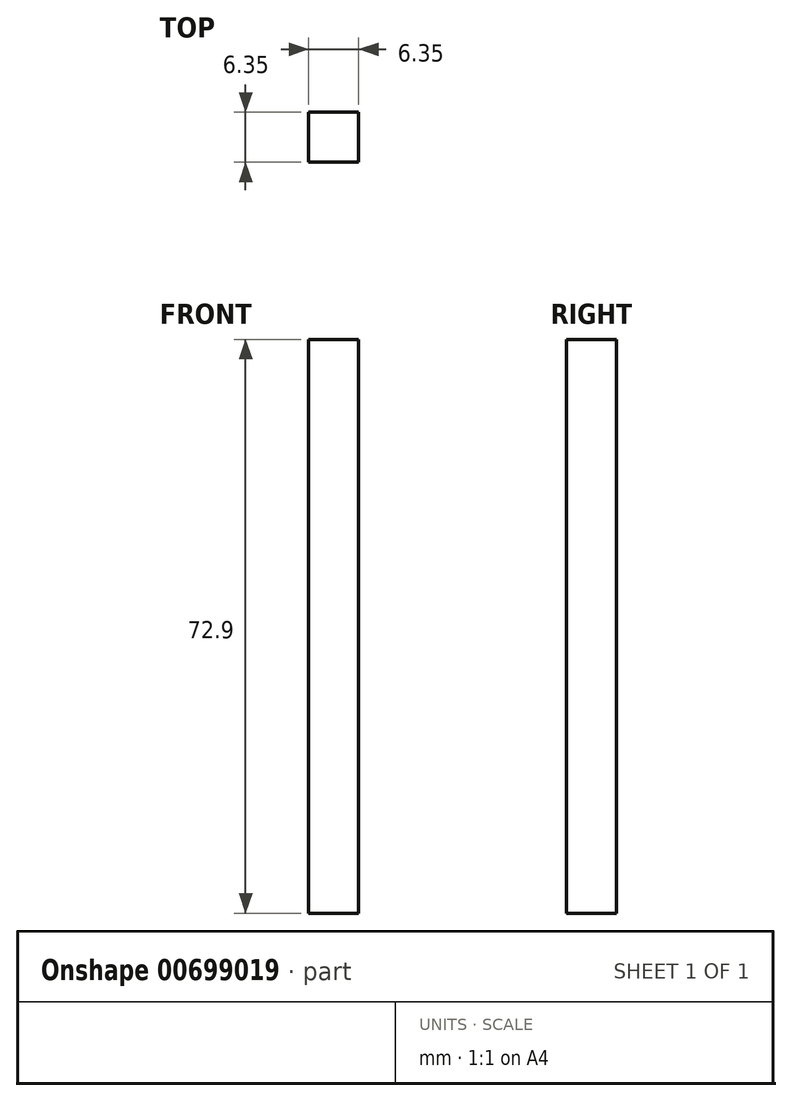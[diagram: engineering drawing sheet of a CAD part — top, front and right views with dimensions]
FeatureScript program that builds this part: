
annotation { "Feature Type Name" : "Feature", "Feature Type Description" : "" }
export const myFeature = defineFeature(function(context is Context, id is Id, definition is map)
    precondition{}
    {
        {
            var Q0;
            Q0=qCreatedBy(makeId("Top.planeOp"),FACE);
            var sketch = newSketch(context, id + "F0", { "sketchPlane" : qUnion([Q0])});
            skLineSegment(sketch, "E0.bottom", {"start": v(-35.74, 0) * mm, "end": v(-29.39, 0) * mm});
            skLineSegment(sketch, "E0.top", {"start": v(-35.74, 6.35) * mm, "end": v(-29.39, 6.35) * mm});
            skLineSegment(sketch, "E0.left", {"start": v(-35.74, 0) * mm, "end": v(-35.74, 6.35) * mm});
            skLineSegment(sketch, "E0.right", {"start": v(-29.39, 0) * mm, "end": v(-29.39, 6.35) * mm});
            skSolve(sketch);
        }
        {
            var Q0;
            Q0 = qSketchRegion(id + "F0", true);
            extrude(context, id + "F1", {"entities" : qUnion([Q0]), "depth" : 72.9 * mm, "offsetDistance" : 25.4 * mm});
        }
    });
